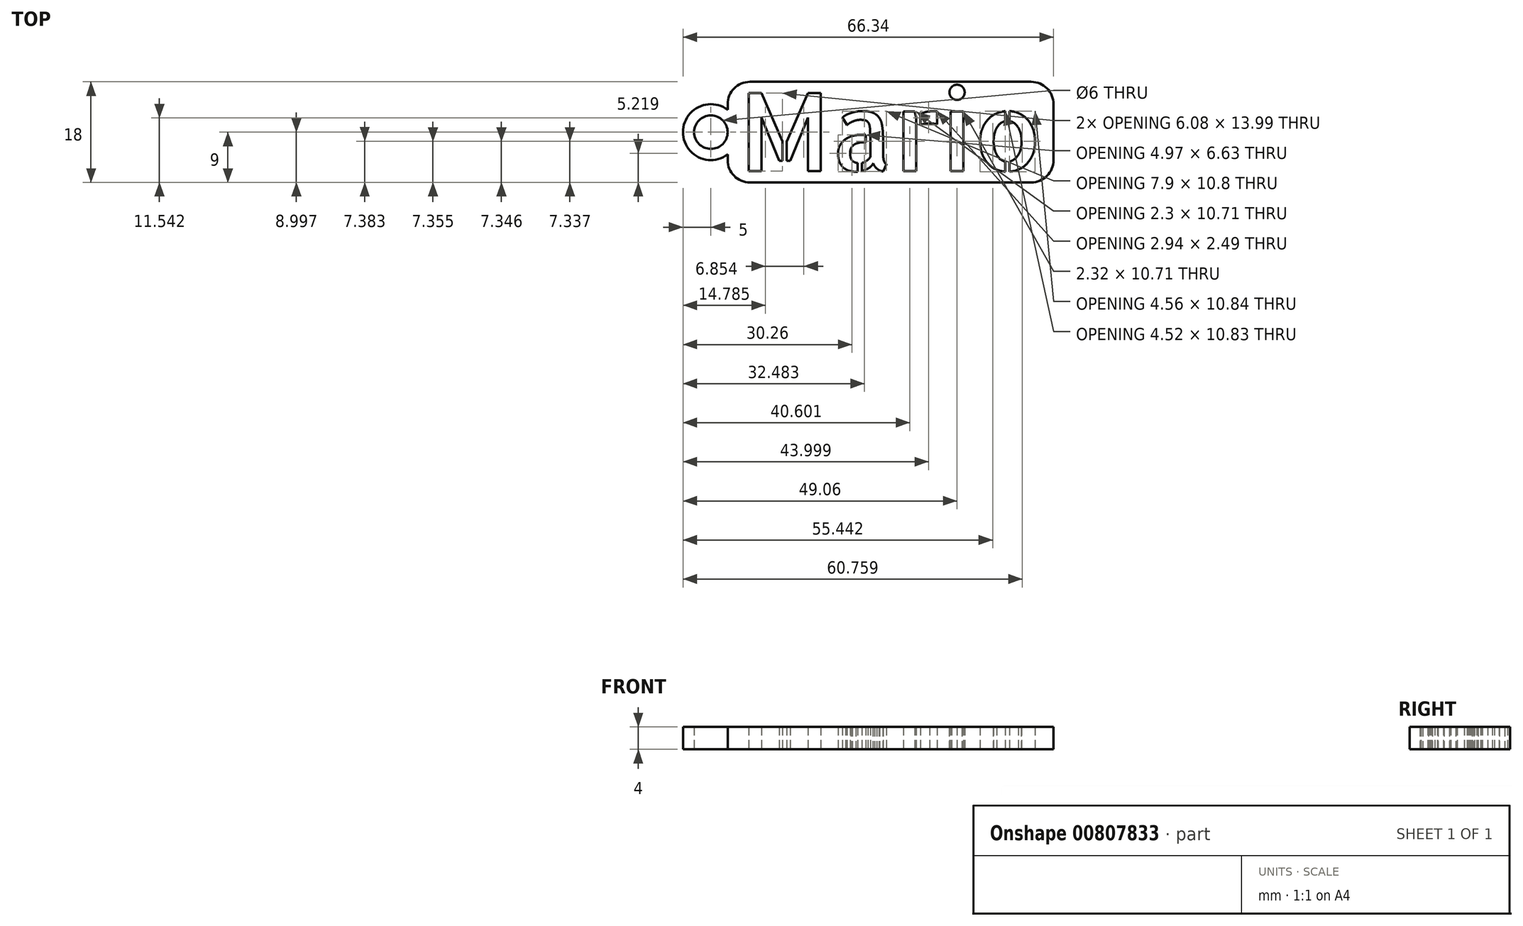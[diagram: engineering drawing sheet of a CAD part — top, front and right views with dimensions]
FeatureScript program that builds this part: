
annotation { "Feature Type Name" : "Feature", "Feature Type Description" : "" }
export const myFeature = defineFeature(function(context is Context, id is Id, definition is map)
    precondition{}
    {
        {
            var Q0;
            Q0=qCreatedBy(makeId("Top.planeOp"),FACE);
            var sketch = newSketch(context, id + "F0", { "sketchPlane" : qUnion([Q0])});
            skLineSegment(sketch, "E0.bottom", {"start": v(-2, -2) * mm, "end": v(56.34, -2) * mm});
            skLineSegment(sketch, "E0.top", {"start": v(-2, 16) * mm, "end": v(56.34, 16) * mm});
            skLineSegment(sketch, "E0.left", {"start": v(-2, -2) * mm, "end": v(-2, 3) * mm});
            skLineSegment(sketch, "E0.right", {"start": v(56.34, -2) * mm, "end": v(56.34, 16) * mm});
            skArc(sketch, "E1", {"start": v(-2, 11) * mm, "mid": v(-10, 7) * mm, "end": v(-2, 3) * mm});
            skLineSegment(sketch, "E2.trimOffspring", {"start": v(-2, 11) * mm, "end": v(-2, 16) * mm});
            skCircle(sketch, "E3", {"center": v(-5, 7) * mm, "radius": 3 * mm});
            skLineSegment(sketch, "E4", {"start": v(56.34, 7) * mm, "end": v(-10, 7) * mm, "construction": true});
            skText(sketch, "E5", { "text": "Mario", "fontName": "AllertaStencil-Regular.ttf"});
            const initialGuessF0  = {"E5": [0, 0, 1, 0, 0.014]};
            skSetInitialGuess(sketch, initialGuessF0);
            skSolve(sketch);
        }
        {
            var Q0;
            Q0=makeQuery(id+"F0.imprint","IMPRINT",FACE,{"disambiguationData":[TD([[makeQuery(id+"F0.imprint","IMPRINT",EDGE,{"derivedFrom":sQuery(id+"F0.wireOp",EDGE,"E0.bottom")}),1.0]])]});
            extrude(context, id + "F1", {"entities" : qUnion([Q0]), "depth" : 4 * mm, "offsetDistance" : 25 * mm});
        }
        {
            var Q0;
            Q0=makeQuery(id+"F1.opExtrude","SWEPT_EDGE",EDGE,{"disambiguationData":[OSD([sQuery(id+"F0.wireOp",EDGE,"E0.bottom"),sQuery(id+"F0.wireOp",EDGE,"E0.left")])]});
            var Q1;
            Q1=makeQuery(id+"F1.opExtrude","SWEPT_EDGE",EDGE,{"disambiguationData":[OSD([sQuery(id+"F0.wireOp",EDGE,"E0.bottom"),sQuery(id+"F0.wireOp",EDGE,"E0.right")])]});
            var Q2;
            Q2=makeQuery(id+"F1.opExtrude","SWEPT_EDGE",EDGE,{"disambiguationData":[OSD([sQuery(id+"F0.wireOp",EDGE,"E0.top"),sQuery(id+"F0.wireOp",EDGE,"E0.right")])]});
            var Q3;
            Q3=makeQuery(id+"F1.opExtrude","SWEPT_EDGE",EDGE,{"disambiguationData":[OSD([sQuery(id+"F0.wireOp",EDGE,"E0.top"),sQuery(id+"F0.wireOp",EDGE,"E2.trimOffspring")])]});
            fillet(context, id + "F2", {"entities" : qUnion([Q0, Q1, Q2, Q3]), "radius" : 4 * mm, "tangentPropagation" : true, "allowEdgeOverflow" : false});
        }
    });
